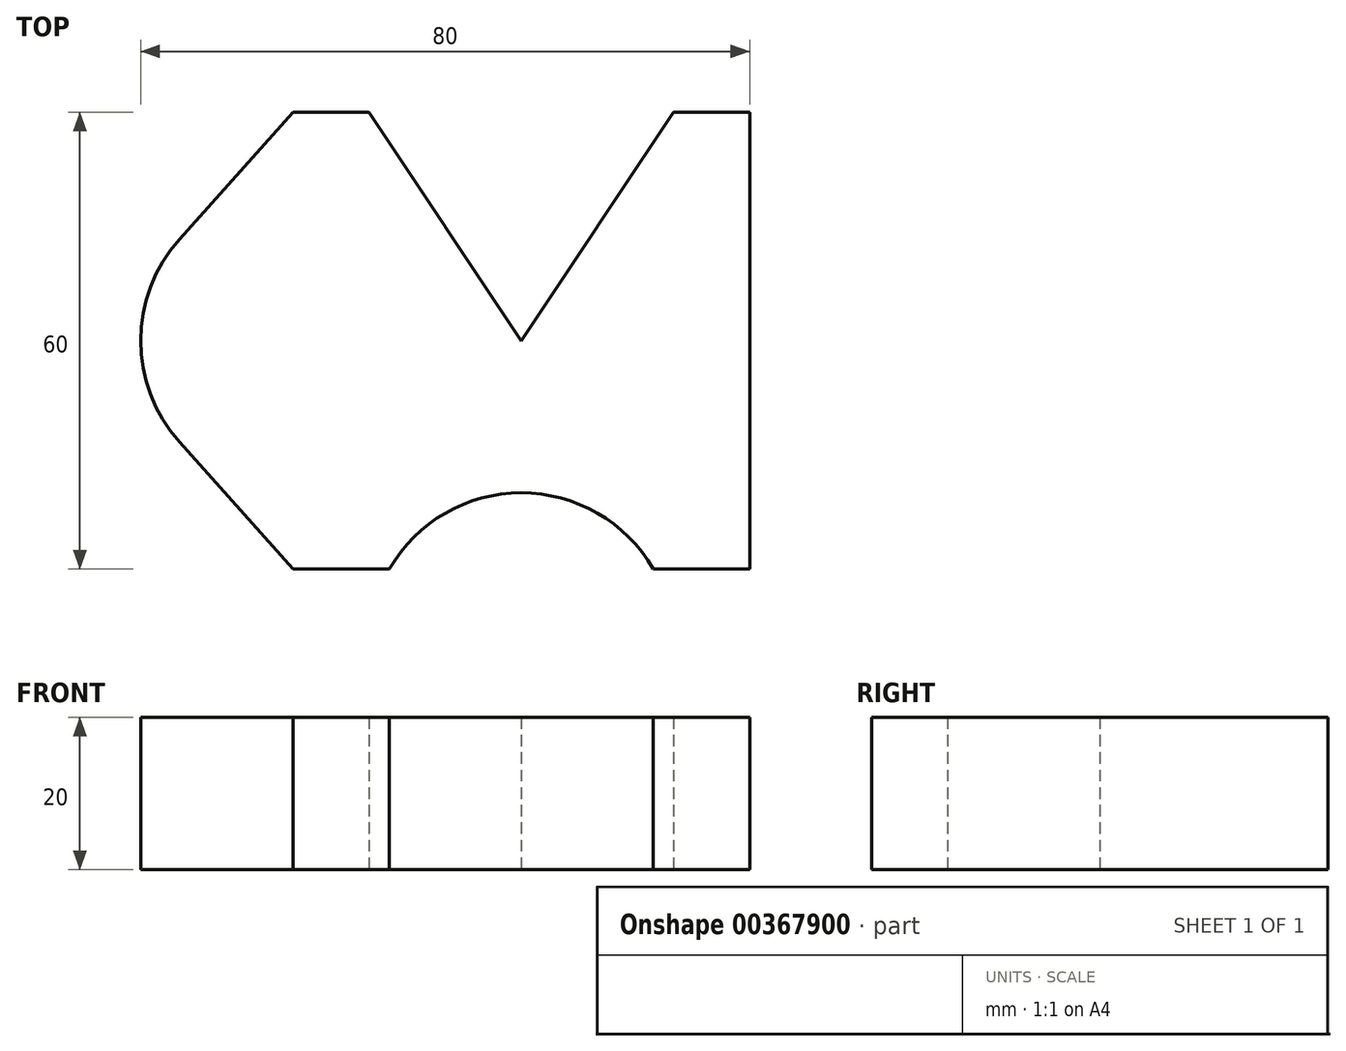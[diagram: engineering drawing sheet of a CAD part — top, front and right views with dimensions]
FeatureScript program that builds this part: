
annotation { "Feature Type Name" : "Feature", "Feature Type Description" : "" }
export const myFeature = defineFeature(function(context is Context, id is Id, definition is map)
    precondition{}
    {
        {
            var Q0;
            Q0=qCreatedBy(makeId("Top.planeOp"),FACE);
            var sketch = newSketch(context, id + "F0", { "sketchPlane" : qUnion([Q0])});
            skLineSegment(sketch, "E0", {"start": v(0, 0) * mm, "end": v(20, 30) * mm});
            skLineSegment(sketch, "E1", {"start": v(20, 30) * mm, "end": v(30, 30) * mm});
            skLineSegment(sketch, "E2", {"start": v(30, -30) * mm, "end": v(17.32, -30) * mm});
            skArc(sketch, "E3", {"start": v(17.32, -30) * mm, "mid": v(0, -20) * mm, "end": v(-17.32, -30) * mm});
            skLineSegment(sketch, "E4", {"start": v(-17.32, -30) * mm, "end": v(-30, -30) * mm});
            skLineSegment(sketch, "E5", {"start": v(-30, -30) * mm, "end": v(-44.9, -13.33) * mm});
            skLineSegment(sketch, "E6", {"start": v(0, 0) * mm, "end": v(-20, 30) * mm});
            skLineSegment(sketch, "E7", {"start": v(-20, 30) * mm, "end": v(-30, 30) * mm});
            skLineSegment(sketch, "E8", {"start": v(-30, 30) * mm, "end": v(-44.9, 13.33) * mm});
            skArc(sketch, "E9", {"start": v(-44.9, 13.33) * mm, "mid": v(-50, 0) * mm, "end": v(-44.9, -13.33) * mm});
            skLineSegment(sketch, "E10", {"start": v(30, 30) * mm, "end": v(30, 0) * mm});
            skLineSegment(sketch, "E11", {"start": v(30, 0) * mm, "end": v(30, -30) * mm});
            skLineSegment(sketch, "E12", {"start": v(-30, 30) * mm, "end": v(-30, -30) * mm, "construction": true});
            skSolve(sketch);
        }
        {
            var Q0;
            Q0 = qSketchRegion(id + "F0", true);
            extrude(context, id + "F1", {"entities" : qUnion([Q0]), "depth" : 20 * mm});
        }
    });
